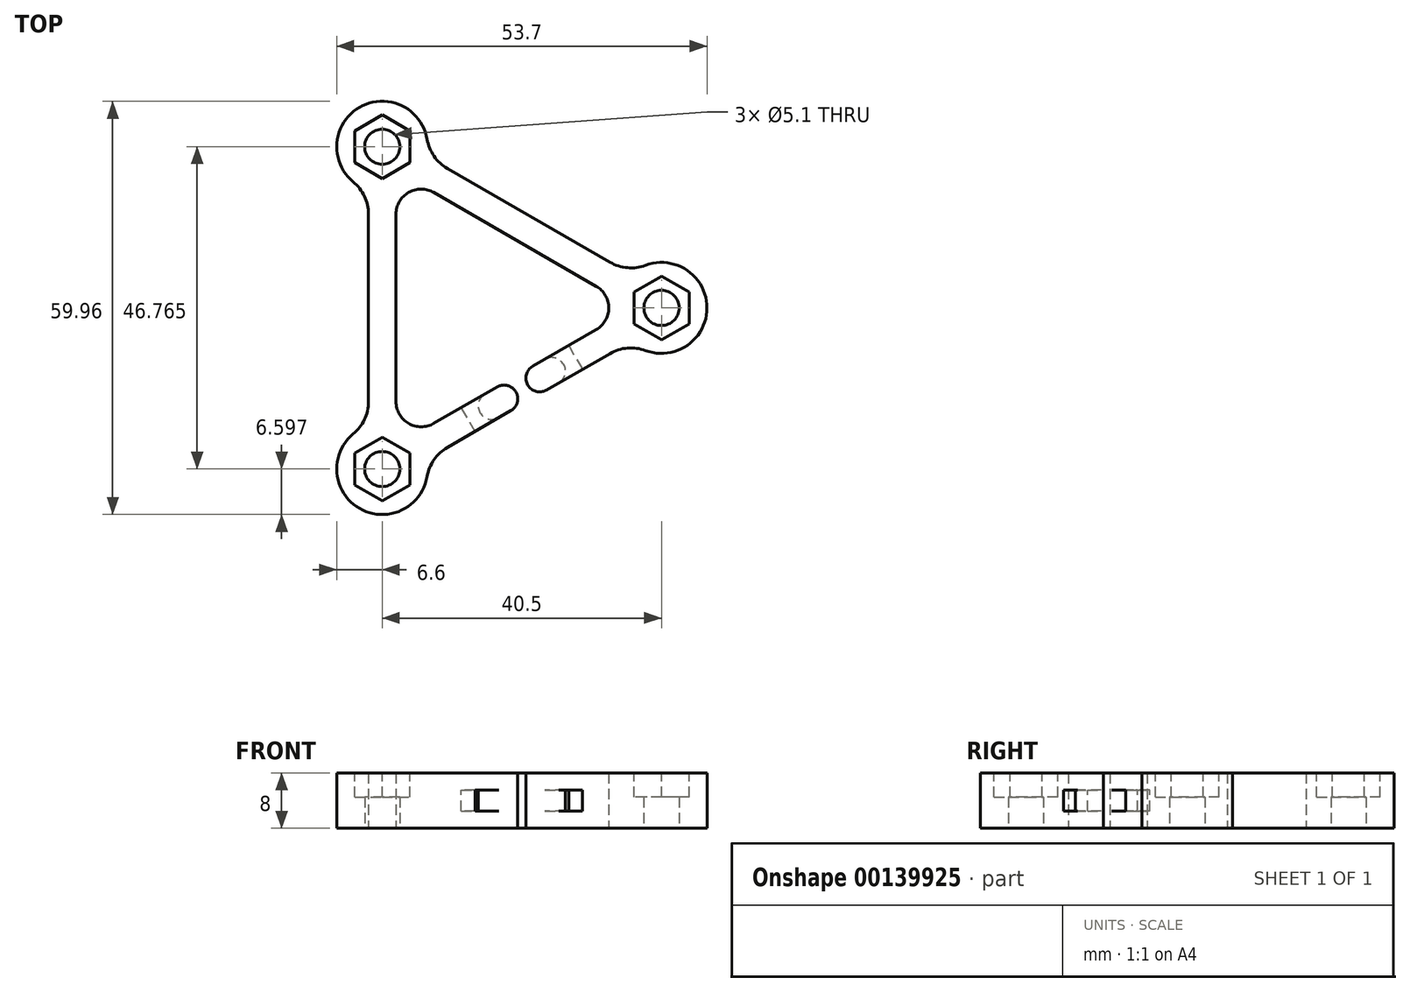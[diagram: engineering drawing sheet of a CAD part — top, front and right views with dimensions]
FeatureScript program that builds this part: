
annotation { "Feature Type Name" : "Feature", "Feature Type Description" : "" }
export const myFeature = defineFeature(function(context is Context, id is Id, definition is map)
    precondition{}
    {
        {
            var Q0;
            Q0=qCreatedBy(makeId("Top.planeOp"),FACE);
            var sketch = newSketch(context, id + "F0", { "sketchPlane" : qUnion([Q0])});
            skCircle(sketch, "E0", {"center": v(-40.5, 23.38) * mm, "radius": 2.55 * mm});
            skCircle(sketch, "E1", {"center": v(-40.5, -23.38) * mm, "radius": 2.55 * mm});
            skCircle(sketch, "E2", {"center": v(0, 0) * mm, "radius": 2.55 * mm});
            skArc(sketch, "E3", {"start": v(-34, 24.49) * mm, "mid": v(-43.8, 29.1) * mm, "end": v(-44.7, 18.3) * mm});
            skArc(sketch, "E4", {"start": v(-44.7, -18.3) * mm, "mid": v(-43.8, -29.1) * mm, "end": v(-34, -24.49) * mm});
            skArc(sketch, "E5", {"start": v(-2.3, -6.19) * mm, "mid": v(6.6, 0) * mm, "end": v(-2.3, 6.19) * mm});
            skLineSegment(sketch, "E6", {"start": v(-33.03, 16.76) * mm, "end": v(-9.47, 3.16) * mm});
            skLineSegment(sketch, "E7", {"start": v(-31.03, 20.22) * mm, "end": v(-7.47, 6.62) * mm});
            skLineSegment(sketch, "E8", {"start": v(-40.5, 23.38) * mm, "end": v(0, 0) * mm, "construction": true});
            skLineSegment(sketch, "E9", {"start": v(0, 0) * mm, "end": v(-40.5, -23.38) * mm, "construction": true});
            skLineSegment(sketch, "E10", {"start": v(-40.5, -23.38) * mm, "end": v(-40.5, 23.38) * mm, "construction": true});
            skArc(sketch, "E11", {"start": v(-33.03, 16.76) * mm, "mid": v(-36.68, 16.76) * mm, "end": v(-38.5, 13.6) * mm});
            skArc(sketch, "E12", {"start": v(-38.5, -13.6) * mm, "mid": v(-36.68, -16.76) * mm, "end": v(-33.03, -16.76) * mm});
            skArc(sketch, "E13", {"start": v(-9.47, -3.16) * mm, "mid": v(-7.65, 0) * mm, "end": v(-9.47, 3.16) * mm});
            skArc(sketch, "E14", {"start": v(-44.7, -18.3) * mm, "mid": v(-43.08, -16.2) * mm, "end": v(-42.5, -13.6) * mm});
            skArc(sketch, "E15", {"start": v(-31.03, -20.22) * mm, "mid": v(-32.99, -22.02) * mm, "end": v(-34, -24.49) * mm});
            skArc(sketch, "E16", {"start": v(-42.5, 13.6) * mm, "mid": v(-43.08, 16.2) * mm, "end": v(-44.7, 18.3) * mm});
            skArc(sketch, "E17", {"start": v(-34, 24.49) * mm, "mid": v(-32.99, 22.02) * mm, "end": v(-31.03, 20.22) * mm});
            skArc(sketch, "E18", {"start": v(-7.47, 6.62) * mm, "mid": v(-4.93, 5.83) * mm, "end": v(-2.3, 6.19) * mm});
            skArc(sketch, "E19", {"start": v(-2.3, -6.19) * mm, "mid": v(-4.93, -5.83) * mm, "end": v(-7.47, -6.62) * mm});
            skLineSegment(sketch, "E20", {"start": v(-33.03, 16.76) * mm, "end": v(-31.03, 20.22) * mm, "construction": true});
            skLineSegment(sketch, "E21", {"start": v(-9.47, 3.16) * mm, "end": v(-7.47, 6.62) * mm, "construction": true});
            skLineSegment(sketch, "E22", {"start": v(-9.47, -3.16) * mm, "end": v(-7.47, -6.62) * mm, "construction": true});
            skLineSegment(sketch, "E23", {"start": v(-42.5, -13.6) * mm, "end": v(-38.5, -13.6) * mm, "construction": true});
            skLineSegment(sketch, "E24", {"start": v(-31.03, -20.22) * mm, "end": v(-33.03, -16.76) * mm, "construction": true});
            skLineSegment(sketch, "E25", {"start": v(-42.5, -13.6) * mm, "end": v(-42.5, 13.6) * mm});
            skLineSegment(sketch, "E26", {"start": v(-38.5, -13.6) * mm, "end": v(-38.5, 13.6) * mm});
            skLineSegment(sketch, "E27", {"start": v(-42.5, 13.6) * mm, "end": v(-38.5, 13.6) * mm, "construction": true});
            skLineSegment(sketch, "E28", {"start": v(-33.03, -16.76) * mm, "end": v(-23.85, -11.46) * mm});
            skLineSegment(sketch, "E29", {"start": v(-18.65, -8.46) * mm, "end": v(-9.47, -3.16) * mm});
            skLineSegment(sketch, "E30", {"start": v(-31.03, -20.22) * mm, "end": v(-21.85, -14.92) * mm});
            skLineSegment(sketch, "E31", {"start": v(-7.47, -6.62) * mm, "end": v(-16.65, -11.92) * mm});
            skArc(sketch, "E32", {"start": v(-21.85, -14.92) * mm, "mid": v(-21.12, -12.2) * mm, "end": v(-23.85, -11.46) * mm});
            skArc(sketch, "E33", {"start": v(-18.65, -8.46) * mm, "mid": v(-19.38, -11.2) * mm, "end": v(-16.65, -11.92) * mm});
            skSolve(sketch);
        }
        {
            var Q0;
            Q0=makeQuery(id+"F0.imprint","IMPRINT",FACE,{"disambiguationData":[TD([[makeQuery(id+"F0.imprint","IMPRINT",EDGE,{"derivedFrom":sQuery(id+"F0.wireOp",EDGE,"E0")}),-1.0]])]});
            extrude(context, id + "F1", {"entities" : qUnion([Q0]), "depth" : 8 * mm, "offsetDistance" : 25 * mm});
        }
        {
            var Q0;
            Q0=makeQuery(id+"F1.opExtrude","CAP_FACE",FACE,{"disambiguationData":[OSD([sQuery(id+"F0.wireOp",EDGE,"E0"),sQuery(id+"F0.wireOp",EDGE,"E1"),sQuery(id+"F0.wireOp",EDGE,"E2"),sQuery(id+"F0.wireOp",EDGE,"E3"),sQuery(id+"F0.wireOp",EDGE,"E4"),sQuery(id+"F0.wireOp",EDGE,"E5"),sQuery(id+"F0.wireOp",EDGE,"T5Vw66OG-G5OR-DHDx-KvU7-dnTMRq0o1A0g"),sQuery(id+"F0.wireOp",EDGE,"8mzCXc7P-Lu7A-tcA2-hDls-zUZMRrlwUirj"),sQuery(id+"F0.wireOp",EDGE,"n4Ubmgs8-MzYA-ilAs-um63-DOsCIZ42xYd5"),sQuery(id+"F0.wireOp",EDGE,"iCspHw3C-Pdpp-QPBW-yDHl-MGOv44Ga2VXa"),sQuery(id+"F0.wireOp",EDGE,"xnWTmErK-ZSIG-ryMW-Ekzr-RR3PqCajZfuL"),sQuery(id+"F0.wireOp",EDGE,"AKW5OVUo-PFRE-jSi0-v7oE-Iw4JobIG5vWv"),sQuery(id+"F0.wireOp",EDGE,"E6"),sQuery(id+"F0.wireOp",EDGE,"JkiSf5jC-OJZR-1wmq-AVkU-QwjWYPwXVpW3"),sQuery(id+"F0.wireOp",EDGE,"9YlTFYq7-sXvY-dmJ4-6YRE-gBgDyT6P94yA")])],"isStart":false});
            var sketch = newSketch(context, id + "F2", { "sketchPlane" : qUnion([Q0])});
            skCircle(sketch, "E34.cCircle", {"center": v(-40.5, 23.38) * mm, "radius": 4 * mm, "construction": true});
            skLineSegment(sketch, "E34.0", {"start": v(-36.5, 25.7) * mm, "end": v(-36.5, 21.07) * mm});
            skLineSegment(sketch, "E34.1", {"start": v(-36.5, 21.07) * mm, "end": v(-40.5, 18.76) * mm});
            skLineSegment(sketch, "E34.2", {"start": v(-40.5, 18.76) * mm, "end": v(-44.5, 21.07) * mm});
            skLineSegment(sketch, "E34.3", {"start": v(-44.5, 21.07) * mm, "end": v(-44.5, 25.7) * mm});
            skLineSegment(sketch, "E34.4", {"start": v(-44.5, 25.7) * mm, "end": v(-40.5, 28) * mm});
            skLineSegment(sketch, "E34.5", {"start": v(-40.5, 28) * mm, "end": v(-36.5, 25.7) * mm});
            skPoint(sketch, "E34.0.midPoint", {"position": v(-36.5, 23.38) * mm});
            skCircle(sketch, "E35.cCircle", {"center": v(-40.5, -23.38) * mm, "radius": 4 * mm, "construction": true});
            skLineSegment(sketch, "E35.0", {"start": v(-36.5, -21.07) * mm, "end": v(-36.5, -25.7) * mm});
            skLineSegment(sketch, "E35.1", {"start": v(-36.5, -25.7) * mm, "end": v(-40.5, -28) * mm});
            skLineSegment(sketch, "E35.2", {"start": v(-40.5, -28) * mm, "end": v(-44.5, -25.7) * mm});
            skLineSegment(sketch, "E35.3", {"start": v(-44.5, -25.7) * mm, "end": v(-44.5, -21.07) * mm});
            skLineSegment(sketch, "E35.4", {"start": v(-44.5, -21.07) * mm, "end": v(-40.5, -18.76) * mm});
            skLineSegment(sketch, "E35.5", {"start": v(-40.5, -18.76) * mm, "end": v(-36.5, -21.07) * mm});
            skPoint(sketch, "E35.0.midPoint", {"position": v(-36.5, -23.38) * mm});
            skCircle(sketch, "E36.cCircle", {"center": v(0, 0) * mm, "radius": 4 * mm, "construction": true});
            skLineSegment(sketch, "E36.0", {"start": v(-4, -2.3) * mm, "end": v(-4, 2.3) * mm});
            skLineSegment(sketch, "E36.1", {"start": v(-4, 2.3) * mm, "end": v(0, 4.62) * mm});
            skLineSegment(sketch, "E36.2", {"start": v(0, 4.62) * mm, "end": v(4, 2.3) * mm});
            skLineSegment(sketch, "E36.3", {"start": v(4, 2.3) * mm, "end": v(4, -2.3) * mm});
            skLineSegment(sketch, "E36.4", {"start": v(4, -2.3) * mm, "end": v(0, -4.62) * mm});
            skLineSegment(sketch, "E36.5", {"start": v(0, -4.62) * mm, "end": v(-4, -2.3) * mm});
            skPoint(sketch, "E36.0.midPoint", {"position": v(-4, 0) * mm});
            skLineSegment(sketch, "E37", {"start": v(-40.5, -23.38) * mm, "end": v(-27, 0) * mm, "construction": true});
            skLineSegment(sketch, "E38", {"start": v(-27, 0) * mm, "end": v(-40.5, 23.38) * mm, "construction": true});
            skLineSegment(sketch, "E39", {"start": v(-27, 0) * mm, "end": v(0, 0) * mm, "construction": true});
            skLineSegment(sketch, "E40", {"start": v(-35, 0) * mm, "end": v(-23, 6.93) * mm, "construction": true});
            skPoint(sketch, "E40.startSnap0", {"position": v(-13.5, 0) * mm});
            skLineSegment(sketch, "E41", {"start": v(-23, 6.93) * mm, "end": v(-23, -6.93) * mm, "construction": true});
            skLineSegment(sketch, "E42", {"start": v(-23, -6.93) * mm, "end": v(-35, 0) * mm, "construction": true});
            skPoint(sketch, "E43", {"position": v(-29, 3.46) * mm});
            skPoint(sketch, "E44", {"position": v(-29, -3.46) * mm});
            skPoint(sketch, "E45", {"position": v(-23, 0) * mm});
            skSolve(sketch);
        }
        {
            var Q0;
            Q0=qSketchRegion(id+"F2",true);
            extrude(context, id + "F3", {"entities" : qUnion([Q0]), "operationType" : NewBodyOperationType.REMOVE, "oppositeDirection" : true, "depth" : 3.5 * mm, "offsetDistance" : 25 * mm});
        }
        {
            var Q0;
            Q0=qCreatedBy(makeId("Top.planeOp"),FACE);
            var Q1;
            Q1=makeQuery(id+"F2.imprint","IMPRINT",FACE,{"disambiguationData":[TD([[makeQuery(id+"F2.imprint","IMPRINT",EDGE,{"derivedFrom":sQuery(id+"F2.wireOp",EDGE,"E34.0")}),1.0]])]});
            cPlane(context, id + "F4", {"entities" : qUnion([Q0, Q1]), "cplaneType" : CPlaneType.MID_PLANE, "offset" : 3 * mm, "oppositeDirection" : true, "width" : 150 * mm, "height" : 150 * mm});
        }
        {
            var Q0;
            Q0=qCreatedBy(id+"F4.planeOp",FACE);
            var sketch = newSketch(context, id + "F5", { "sketchPlane" : qUnion([Q0])});
            skArc(sketch, "E46", {"start": v(-25.58, -12.46) * mm, "mid": v(-26.31, -15.2) * mm, "end": v(-23.58, -15.92) * mm});
            skArc(sketch, "E47", {"start": v(-14.92, -10.92) * mm, "mid": v(-14.19, -8.2) * mm, "end": v(-16.92, -7.46) * mm});
            skLineSegment(sketch, "E48", {"start": v(-16.92, -7.46) * mm, "end": v(-13.46, -5.46) * mm});
            skLineSegment(sketch, "E49", {"start": v(-13.46, -5.46) * mm, "end": v(-11.46, -8.92) * mm});
            skLineSegment(sketch, "E50", {"start": v(-11.46, -8.92) * mm, "end": v(-14.92, -10.92) * mm});
            skLineSegment(sketch, "E51", {"start": v(-23.58, -15.92) * mm, "end": v(-27.04, -17.92) * mm});
            skLineSegment(sketch, "E52", {"start": v(-27.04, -17.92) * mm, "end": v(-29.04, -14.46) * mm});
            skLineSegment(sketch, "E53", {"start": v(-29.04, -14.46) * mm, "end": v(-25.58, -12.46) * mm});
            skSolve(sketch);
        }
        {
            var Q0;
            Q0 = qSketchRegion(id + "F5", true);
            extrude(context, id + "F6", {"entities" : qUnion([Q0]), "operationType" : NewBodyOperationType.REMOVE, "oppositeDirection" : true, "depth" : 3 * mm, "offsetDistance" : 25 * mm, "symmetric" : true});
        }
    });
